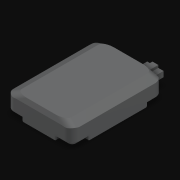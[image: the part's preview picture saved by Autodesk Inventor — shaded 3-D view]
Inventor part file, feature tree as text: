
AUTODESK INVENTOR PART (.ipt)
format: ipt  version: 2021 (Build 250183000, 183)  size: 418,816 bytes
history: native  units: in
note: dims shown in document units (in); Inventor stores cm internally (conversion verified against a paired STEP export)
features: extrude x5, chamfer x4, fillet x4, sketch x4
ambient origin geometry x8: Origin, YZ Plane, XZ Plane, XY Plane, X Axis, Y Axis, Z Axis, Center Point
bodies: Solid1 (feature_tree)
feature tree (17):
  extrude  "Extrusion1"  Depth=3.93in
  chamfer  "Chamfer2"  Distance=1.239in
  chamfer  "Chamfer3"  Distance=0.115in Angle=45.0deg
  chamfer  "Chamfer4"  Distance=0.115in Angle=45.0deg
  chamfer  "Chamfer5"  Distance=0.5in Angle=45.0deg
  fillet  "Fillet5"  Radius=0.465in
  fillet  "Fillet6"  Radius=0.25in
  extrude  "Extrusion4"  Depth=0.5in
  extrude  "Extrusion5"  Depth=0.625in
  fillet  "Fillet7"  Radius=0.314in
  fillet  "Fillet8"  Radius=1.239in
  extrude  "Extrusion6"  Depth=0.079in
  extrude  "Extrusion7"  Depth=0.625in
  sketch  "Sketch4"  dims[d0=5.43in d1=3.93in d2=1.239in d3=0.0in d20=0.115in d21=0.25in d22=45.0deg d23=0.115in d24=0.25in d25=45.0deg d26=0.5in d27=0.25in d28=45.0deg]
  sketch  "Sketch5"  dims[d29=0.5in d30=0.25in d31=45.0deg d32=0.465in d33=0.25in]
  sketch  "Sketch6"  dims[d34=3.5in d35=0.5in]
  sketch  "Sketch7"  dims[d36=1.239in d37=0.0in d38=2.0in d39=0.314in d40=1.239in d41=0.0in d42=0.079in d43=0.01in d44=0.136in d45=0.7874in d47=3.0in d48=0.7874in d50=1.5in d53=0.171in d54=0.171in d55=0.25in d56=0.0in d57=0.972in d58=0.324in d59=0.348in d60=0.153in d61=0.313in d62=0.6125in d63=0.4345in d64=0.625in d65=0.0in d66=1.965in d67=2.715in]
